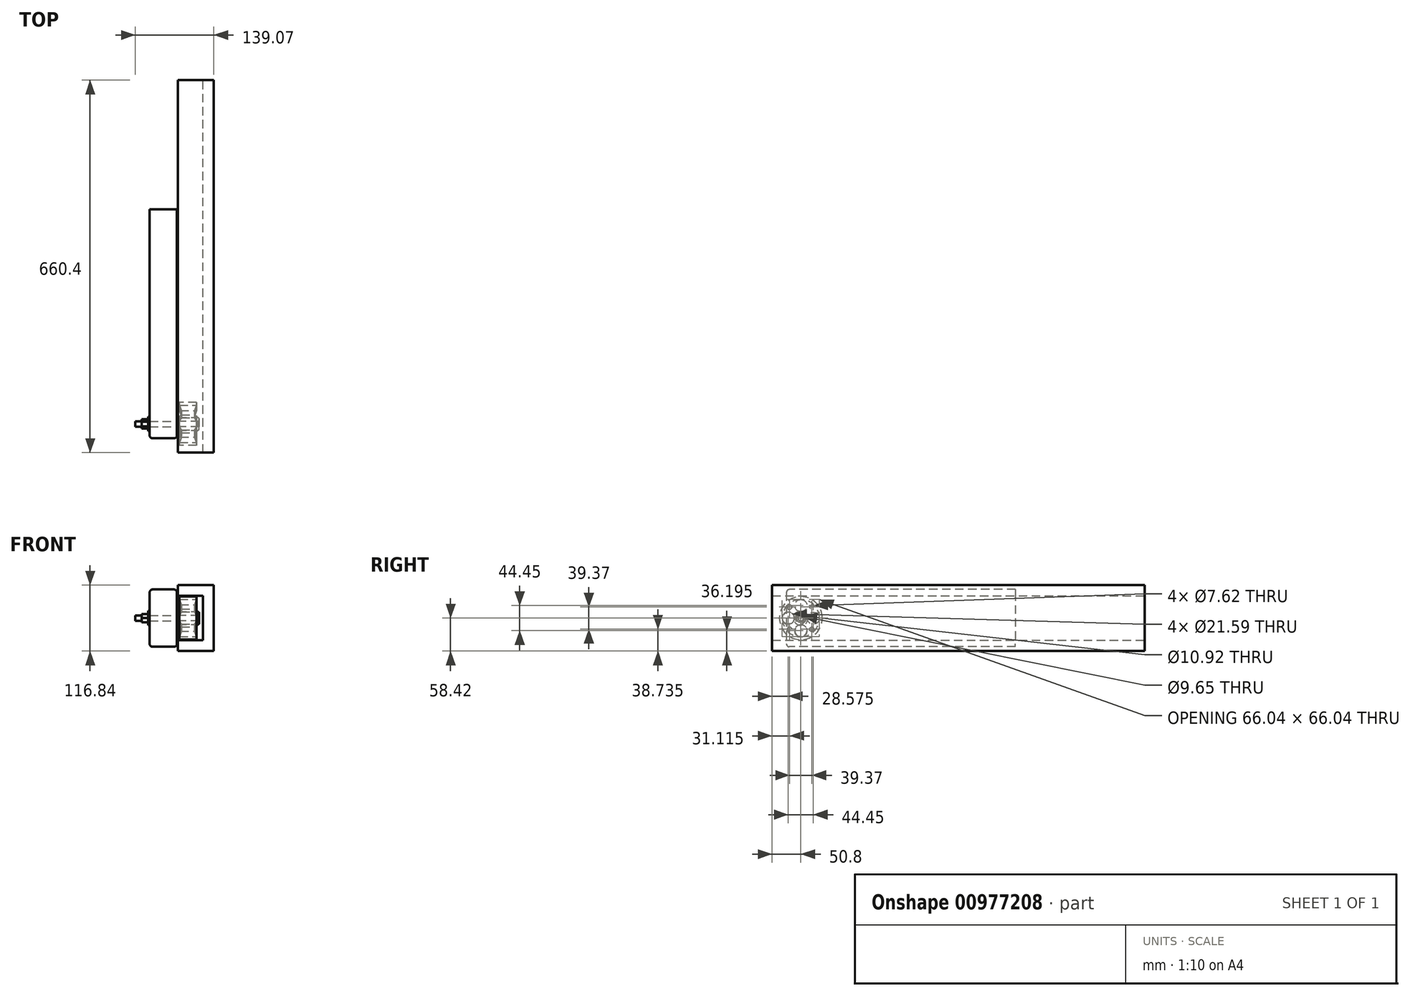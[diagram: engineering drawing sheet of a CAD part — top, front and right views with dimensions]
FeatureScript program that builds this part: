
annotation { "Feature Type Name" : "Feature", "Feature Type Description" : "" }
export const myFeature = defineFeature(function(context is Context, id is Id, definition is map)
    precondition{}
    {
        {
            var Q0;
            Q0=qCreatedBy(makeId("Front.planeOp"),FACE);
            var sketch = newSketch(context, id + "F0", { "sketchPlane" : qUnion([Q0])});
            skLineSegment(sketch, "E0", {"start": v(-15.24, 38.1) * mm, "end": v(15.24, 38.1) * mm});
            skLineSegment(sketch, "E1", {"start": v(-19.69, 4.83) * mm, "end": v(19.69, 4.83) * mm});
            skLineSegment(sketch, "E2", {"start": v(15.24, 38.1) * mm, "end": v(15.24, 33.02) * mm});
            skLineSegment(sketch, "E3", {"start": v(-15.24, 38.1) * mm, "end": v(-15.24, 33.02) * mm});
            skLineSegment(sketch, "E4", {"start": v(0, 22.84) * mm, "end": v(0, -22.84) * mm, "construction": true});
            skLineSegment(sketch, "E5", {"start": v(19.69, 4.83) * mm, "end": v(19.69, 9.9) * mm});
            skLineSegment(sketch, "E6", {"start": v(-19.69, 4.83) * mm, "end": v(-19.69, 9.9) * mm});
            skArc(sketch, "E7", {"start": v(-19.69, 9.9) * mm, "mid": v(-12.22, 20.45) * mm, "end": v(-15.24, 33.02) * mm});
            skArc(sketch, "E8.MirrorCS", {"start": v(19.69, 9.9) * mm, "mid": v(12.22, 20.45) * mm, "end": v(15.24, 33.02) * mm});
            skLineSegment(sketch, "E9", {"start": v(-15.36, 0) * mm, "end": v(15.36, 0) * mm, "construction": true});
            skSolve(sketch);
        }
        {
            var Q0;
            Q0 = qSketchRegion(id + "F0", true);
            var Q1;
            Q1=sQuery(id+"F0.wireOp",EDGE,"E9");
            revolve(context, id + "F1", {"surfaceOperationType" : NewSurfaceOperationType.NEW, "entities" : qUnion([Q0]), "axis" : qUnion([Q1]), "revolveType" : RevolveType.FULL});
        }
        {
            var Q0;
            Q0=qCreatedBy(makeId("Right.planeOp"),FACE);
            var sketch = newSketch(context, id + "F2", { "sketchPlane" : qUnion([Q0])});
            skCircle(sketch, "E10", {"center": v(0, 0) * mm, "radius": 4.83 * mm});
            skCircle(sketch, "E11", {"center": v(0, 22.23) * mm, "radius": 10.8 * mm});
            skCircle(sketch, "E12", {"center": v(-22.23, 0) * mm, "radius": 10.8 * mm});
            skCircle(sketch, "E13", {"center": v(22.23, 0) * mm, "radius": 10.8 * mm});
            skCircle(sketch, "E14", {"center": v(0, -22.23) * mm, "radius": 10.8 * mm});
            skCircle(sketch, "E15", {"center": v(0, 0) * mm, "radius": 22.23 * mm, "construction": true});
            skCircle(sketch, "E16", {"center": v(-19.69, 19.69) * mm, "radius": 3.81 * mm});
            skCircle(sketch, "E17", {"center": v(19.69, 19.69) * mm, "radius": 3.81 * mm});
            skCircle(sketch, "E18", {"center": v(19.69, -19.69) * mm, "radius": 3.81 * mm});
            skCircle(sketch, "E19", {"center": v(-19.69, -19.69) * mm, "radius": 3.81 * mm});
            skLineSegment(sketch, "E20.bottom", {"start": v(19.69, 19.69) * mm, "end": v(-19.69, 19.69) * mm, "construction": true});
            skLineSegment(sketch, "E20.top", {"start": v(19.69, -19.69) * mm, "end": v(-19.69, -19.69) * mm, "construction": true});
            skLineSegment(sketch, "E20.left", {"start": v(19.69, 19.69) * mm, "end": v(19.69, -19.69) * mm, "construction": true});
            skLineSegment(sketch, "E20.right", {"start": v(-19.69, 19.69) * mm, "end": v(-19.69, -19.69) * mm, "construction": true});
            skSolve(sketch);
        }
        {
            var Q0;
            Q0 = qSketchRegion(id + "F2", true);
            extrude(context, id + "F3", {"entities" : qUnion([Q0]), "operationType" : NewBodyOperationType.REMOVE, "endBound" : BoundingType.THROUGH_ALL, "oppositeDirection" : true, "depth" : 25.4 * mm, "offsetDistance" : 25.4 * mm, "hasSecondDirection" : true, "secondDirectionBound" : SecondDirectionBoundingType.THROUGH_ALL, "secondDirectionOppositeDirection" : false, "secondDirectionDepth" : 25.4 * mm});
        }
        {
            var Q0;
            Q0=makeQuery(id+"F1.opRevolve","SWEPT_FACE",FACE,{"disambiguationData":[OSD([sQuery(id+"F0.wireOp",EDGE,"E6")])]});
            var sketch = newSketch(context, id + "F4", { "sketchPlane" : qUnion([Q0])});
            skCircle(sketch, "E21", {"center": v(0, 0) * mm, "radius": 4.76 * mm});
            skSolve(sketch);
        }
        {
            var Q0;
            Q0 = qSketchRegion(id + "F4", true);
            extrude(context, id + "F5", {"entities" : qUnion([Q0]), "depth" : 73.66 * mm, "offsetDistance" : 25.4 * mm});
        }
        {
            var Q0;
            Q0=makeQuery(id+"F5.opExtrude","CAP_FACE",FACE,{"disambiguationData":[OSD([sQuery(id+"F4.wireOp",EDGE,"E21")])],"isStart":true});
            cPlane(context, id + "F6", {"entities" : qUnion([Q0]), "cplaneType" : CPlaneType.OFFSET, "offset" : 50.8 * mm, "oppositeDirection" : true, "width" : 152.4 * mm, "height" : 152.4 * mm});
        }
        {
            var Q0;
            Q0=qCreatedBy(id+"F6.planeOp",FACE);
            var sketch = newSketch(context, id + "F7", { "sketchPlane" : qUnion([Q0])});
            skCircle(sketch, "E22.cCircle", {"center": v(0, 0) * mm, "radius": 7.09 * mm, "construction": true});
            skLineSegment(sketch, "E22.0", {"start": v(-4.1, -7.09) * mm, "end": v(-8.18, 0) * mm});
            skLineSegment(sketch, "E22.1", {"start": v(-8.18, 0) * mm, "end": v(-4.1, 7.09) * mm});
            skLineSegment(sketch, "E22.2", {"start": v(-4.1, 7.09) * mm, "end": v(4.1, 7.09) * mm});
            skLineSegment(sketch, "E22.3", {"start": v(4.1, 7.09) * mm, "end": v(8.18, 0) * mm});
            skLineSegment(sketch, "E22.4", {"start": v(8.18, 0) * mm, "end": v(4.1, -7.09) * mm});
            skLineSegment(sketch, "E22.5", {"start": v(4.1, -7.09) * mm, "end": v(-4.1, -7.09) * mm});
            skPoint(sketch, "E22.0.midPoint", {"position": v(-6.14, -3.54) * mm});
            skSolve(sketch);
        }
        {
            var Q0;
            Q0 = qSketchRegion(id + "F7", true);
            extrude(context, id + "F8", {"entities" : qUnion([Q0]), "operationType" : NewBodyOperationType.ADD, "oppositeDirection" : true, "depth" : 11.43 * mm, "offsetDistance" : 25.4 * mm});
        }
        {
            var Q0;
            Q0=makeQuery(id+"F8.opExtrude","CAP_FACE",FACE,{"disambiguationData":[OSD([sQuery(id+"F7.wireOp",EDGE,"E22.0"),sQuery(id+"F7.wireOp",EDGE,"E22.1"),sQuery(id+"F7.wireOp",EDGE,"E22.2"),sQuery(id+"F7.wireOp",EDGE,"E22.3"),sQuery(id+"F7.wireOp",EDGE,"E22.4"),sQuery(id+"F7.wireOp",EDGE,"E22.5")])],"isStart":true});
            var sketch = newSketch(context, id + "F9", { "sketchPlane" : qUnion([Q0])});
            skCircle(sketch, "E23", {"center": v(0, 0) * mm, "radius": 5.46 * mm});
            skCircle(sketch, "E24", {"center": v(0, 0) * mm, "radius": 12.7 * mm});
            skSolve(sketch);
        }
        {
            var Q0;
            Q0 = qSketchRegion(id + "F9", true);
            extrude(context, id + "F10", {"entities" : qUnion([Q0]), "depth" : 1.78 * mm, "offsetDistance" : 25.4 * mm});
        }
        {
            var Q0;
            Q0=makeQuery(id+"F1.opRevolve","SWEPT_FACE",FACE,{"disambiguationData":[OSD([sQuery(id+"F0.wireOp",EDGE,"E6")])]});
            var sketch = newSketch(context, id + "F11", { "sketchPlane" : qUnion([Q0])});
            skLineSegment(sketch, "E25.bottom", {"start": v(-380.31, 50.8) * mm, "end": v(25.4, 50.8) * mm});
            skLineSegment(sketch, "E25.top", {"start": v(-380.31, -50.8) * mm, "end": v(25.4, -50.8) * mm});
            skLineSegment(sketch, "E25.left", {"start": v(-380.31, 50.8) * mm, "end": v(-380.31, -50.8) * mm});
            skLineSegment(sketch, "E25.right", {"start": v(25.4, 50.8) * mm, "end": v(25.4, -50.8) * mm});
            skLineSegment(sketch, "E26", {"start": v(-380.31, 0) * mm, "end": v(25.4, 0) * mm, "construction": true});
            skSolve(sketch);
        }
        {
            var Q0;
            Q0 = qSketchRegion(id + "F11", true);
            extrude(context, id + "F12", {"entities" : qUnion([Q0]), "depth" : 48.26 * mm, "offsetDistance" : 25.4 * mm});
        }
        {
            var Q0;
            Q0=makeQuery(id+"F12.opExtrude","SWEPT_FACE",FACE,{"disambiguationData":[OSD([sQuery(id+"F11.wireOp",EDGE,"E25.right")])]});
            var Q1;
            Q1=makeQuery(id+"F12.opExtrude","CAP_EDGE",EDGE,{"disambiguationData":[OSD([sQuery(id+"F11.wireOp",EDGE,"E25.bottom")])],"isStart":false});
            var Q2;
            Q2=makeQuery(id+"F12.opExtrude","CAP_EDGE",EDGE,{"disambiguationData":[OSD([sQuery(id+"F11.wireOp",EDGE,"E25.bottom")])],"isStart":true});
            var Q3;
            Q3=makeQuery(id+"F12.opExtrude","CAP_EDGE",EDGE,{"disambiguationData":[OSD([sQuery(id+"F11.wireOp",EDGE,"E25.top")])],"isStart":false});
            var Q4;
            Q4=makeQuery(id+"F12.opExtrude","CAP_EDGE",EDGE,{"disambiguationData":[OSD([sQuery(id+"F11.wireOp",EDGE,"E25.top")])],"isStart":true});
            fillet(context, id + "F13", {"entities" : qUnion([Q0, Q1, Q2, Q3, Q4]), "radius" : 5.08 * mm, "tangentPropagation" : true, "allowEdgeOverflow" : false});
        }
        {
            var Q0;
            Q0=qCreatedBy(makeId("Front.planeOp"),FACE);
            var sketch = newSketch(context, id + "F14", { "sketchPlane" : qUnion([Q0])});
            skLineSegment(sketch, "E27.bottom", {"start": v(-17.78, 39.37) * mm, "end": v(26.67, 39.37) * mm});
            skLineSegment(sketch, "E27.top", {"start": v(-17.78, -39.37) * mm, "end": v(26.67, -39.37) * mm});
            skLineSegment(sketch, "E27.right", {"start": v(26.67, 39.37) * mm, "end": v(26.67, -39.37) * mm});
            skLineSegment(sketch, "E28.bottom", {"start": v(-17.78, 58.42) * mm, "end": v(45.72, 58.42) * mm});
            skLineSegment(sketch, "E28.top", {"start": v(-17.78, -58.42) * mm, "end": v(45.72, -58.42) * mm});
            skLineSegment(sketch, "E28.right", {"start": v(45.72, 58.42) * mm, "end": v(45.72, -58.42) * mm});
            skLineSegment(sketch, "E29", {"start": v(-46.71, 0) * mm, "end": v(46.71, 0) * mm, "construction": true});
            skLineSegment(sketch, "E30", {"start": v(-17.78, 58.42) * mm, "end": v(-17.78, 39.37) * mm});
            skLineSegment(sketch, "E31", {"start": v(-17.78, -39.37) * mm, "end": v(-17.78, -58.42) * mm});
            skSolve(sketch);
        }
        {
            var Q0;
            Q0 = qSketchRegion(id + "F14", true);
            extrude(context, id + "F15", {"entities" : qUnion([Q0]), "depth" : 50.8 * mm, "offsetDistance" : 25.4 * mm, "hasSecondDirection" : true, "secondDirectionOppositeDirection" : true, "secondDirectionDepth" : 609.6 * mm});
        }
    });
